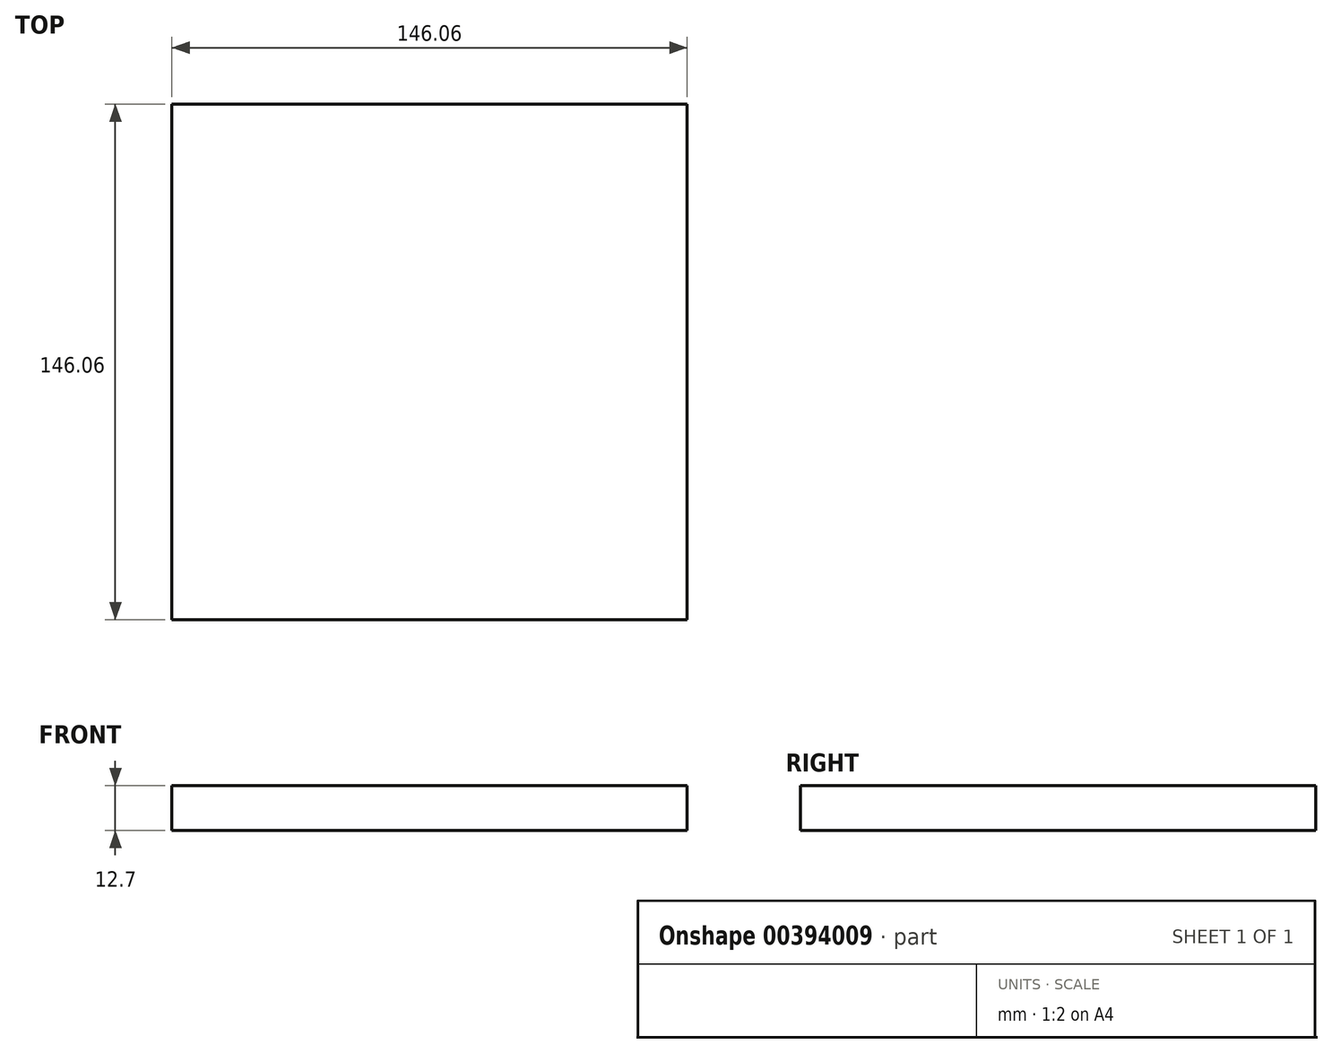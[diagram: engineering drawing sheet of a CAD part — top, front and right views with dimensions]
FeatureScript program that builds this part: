
annotation { "Feature Type Name" : "Feature", "Feature Type Description" : "" }
export const myFeature = defineFeature(function(context is Context, id is Id, definition is map)
    precondition{}
    {
        {
            var Q0;
            Q0=qCreatedBy(makeId("Top.planeOp"),FACE);
            var sketch = newSketch(context, id + "F0", { "sketchPlane" : qUnion([Q0])});
            skLineSegment(sketch, "E0.bottom", {"start": v(73.02, 73.03) * mm, "end": v(-73.03, 73.03) * mm});
            skLineSegment(sketch, "E0.top", {"start": v(73.03, -73.03) * mm, "end": v(-73.02, -73.03) * mm});
            skLineSegment(sketch, "E0.left", {"start": v(73.02, 73.03) * mm, "end": v(73.03, -73.03) * mm});
            skLineSegment(sketch, "E0.right", {"start": v(-73.03, 73.03) * mm, "end": v(-73.02, -73.03) * mm});
            skPoint(sketch, "E0.middle", {"position": v(0, 0) * mm});
            skSolve(sketch);
        }
        {
            var Q0;
            Q0=qSketchRegion(id+"F0",true);
            extrude(context, id + "F1", {"entities" : qUnion([Q0]), "depth" : 12.7 * mm});
        }
    });
